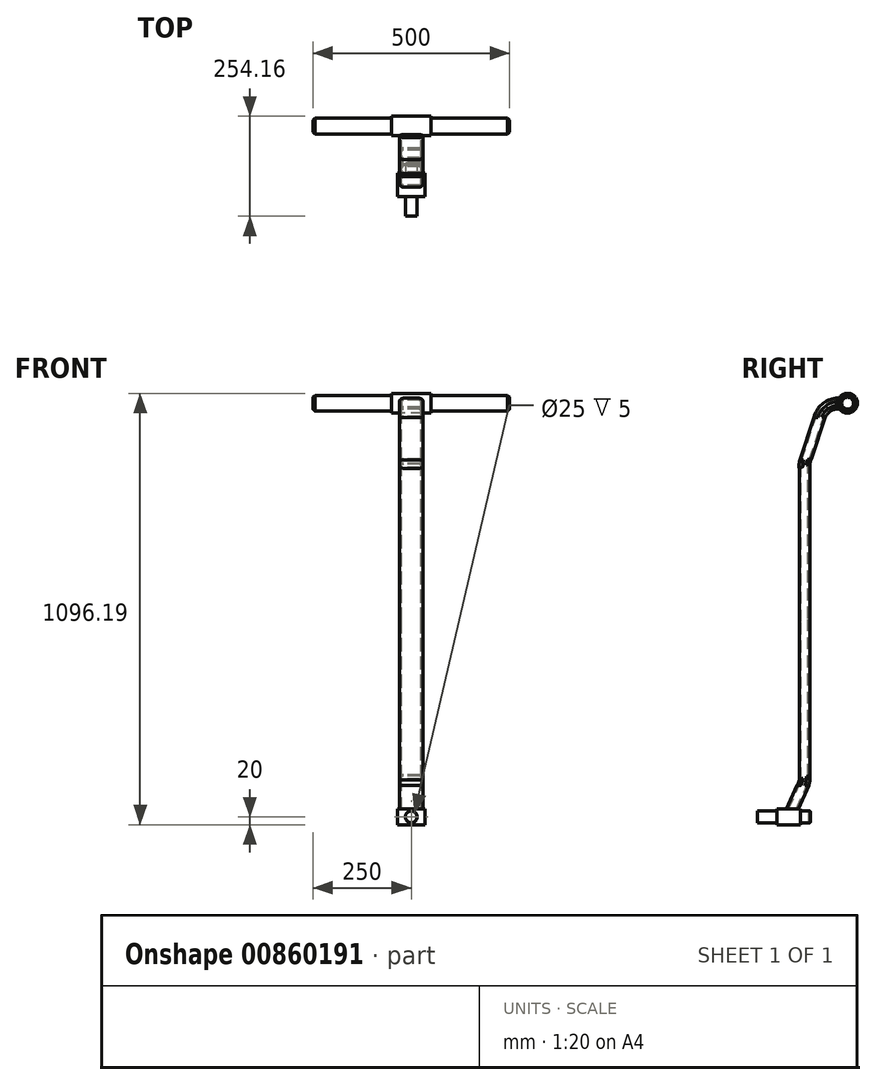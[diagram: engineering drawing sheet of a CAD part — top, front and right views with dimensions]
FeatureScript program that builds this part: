
annotation { "Feature Type Name" : "Feature", "Feature Type Description" : "" }
export const myFeature = defineFeature(function(context is Context, id is Id, definition is map)
    precondition{}
    {
        {
            var Q0;
            Q0=qCreatedBy(makeId("Top.planeOp"),FACE);
            var sketch = newSketch(context, id + "F0", { "sketchPlane" : qUnion([Q0])});
            skLineSegment(sketch, "E0.bottom", {"start": v(20, -15) * mm, "end": v(-20, -15) * mm});
            skLineSegment(sketch, "E0.top", {"start": v(20, 15) * mm, "end": v(-20, 15) * mm});
            skLineSegment(sketch, "E0.left", {"start": v(30, -5) * mm, "end": v(30, 5) * mm});
            skLineSegment(sketch, "E0.right", {"start": v(-30, -5) * mm, "end": v(-30, 5) * mm});
            skPoint(sketch, "E0.middle", {"position": v(0, 0) * mm});
            skPoint(sketch, "E1.visualSharp", {"position": v(-30, 15) * mm});
            skArc(sketch, "E1.filletArc", {"start": v(-20, 15) * mm, "mid": v(-27.07, 12.07) * mm, "end": v(-30, 5) * mm});
            skPoint(sketch, "E2.visualSharp", {"position": v(-30, -15) * mm});
            skArc(sketch, "E2.filletArc", {"start": v(-30, -5) * mm, "mid": v(-27.07, -12.07) * mm, "end": v(-20, -15) * mm});
            skPoint(sketch, "E3.visualSharp", {"position": v(30, -15) * mm});
            skArc(sketch, "E3.filletArc", {"start": v(20, -15) * mm, "mid": v(27.07, -12.07) * mm, "end": v(30, -5) * mm});
            skPoint(sketch, "E4.visualSharp", {"position": v(30, 15) * mm});
            skArc(sketch, "E4.filletArc", {"start": v(30, 5) * mm, "mid": v(27.07, 12.07) * mm, "end": v(20, 15) * mm});
            skLineSegment(sketch, "E5.bottom", {"start": v(20, 10) * mm, "end": v(-20, 10) * mm});
            skLineSegment(sketch, "E5.top", {"start": v(20, -10) * mm, "end": v(-20, -10) * mm});
            skLineSegment(sketch, "E5.left", {"start": v(25, 5) * mm, "end": v(25, -5) * mm});
            skLineSegment(sketch, "E5.right", {"start": v(-25, 5) * mm, "end": v(-25, -5) * mm});
            skPoint(sketch, "E6.visualSharp", {"position": v(-25, 10) * mm});
            skArc(sketch, "E6.filletArc", {"start": v(-20, 10) * mm, "mid": v(-23.54, 8.54) * mm, "end": v(-25, 5) * mm});
            skPoint(sketch, "E7.visualSharp", {"position": v(-25, -10) * mm});
            skArc(sketch, "E7.filletArc", {"start": v(-25, -5) * mm, "mid": v(-23.54, -8.54) * mm, "end": v(-20, -10) * mm});
            skPoint(sketch, "E8.visualSharp", {"position": v(25, -10) * mm});
            skArc(sketch, "E8.filletArc", {"start": v(20, -10) * mm, "mid": v(23.54, -8.54) * mm, "end": v(25, -5) * mm});
            skPoint(sketch, "E9.visualSharp", {"position": v(25, 10) * mm});
            skArc(sketch, "E9.filletArc", {"start": v(25, 5) * mm, "mid": v(23.54, 8.54) * mm, "end": v(20, 10) * mm});
            skSolve(sketch);
        }
        {
            var Q0;
            Q0=qCreatedBy(makeId("Right.planeOp"),FACE);
            var sketch = newSketch(context, id + "F1", { "sketchPlane" : qUnion([Q0])});
            skLineSegment(sketch, "E10", {"start": v(0, 0) * mm, "end": v(35.63, 79.56) * mm});
            skLineSegment(sketch, "E11", {"start": v(40, 100) * mm, "end": v(40, 500) * mm});
            skPoint(sketch, "E12.visualSharp", {"position": v(40, 89.31) * mm});
            skArc(sketch, "E12.filletArc", {"start": v(35.63, 79.56) * mm, "mid": v(38.9, 89.55) * mm, "end": v(40, 100) * mm});
            skLineSegment(sketch, "E13", {"start": v(40, 500) * mm, "end": v(40, 891.89) * mm});
            skLineSegment(sketch, "E14", {"start": v(42.57, 907.7) * mm, "end": v(78.6, 1015.81) * mm});
            skLineSegment(sketch, "E15", {"start": v(126.04, 1050) * mm, "end": v(150, 1050) * mm});
            skPoint(sketch, "E16.visualSharp", {"position": v(40, 900) * mm});
            skArc(sketch, "E16.filletArc", {"start": v(42.57, 907.7) * mm, "mid": v(40.65, 899.9) * mm, "end": v(40, 891.89) * mm});
            skPoint(sketch, "E17.visualSharp", {"position": v(90, 1050) * mm});
            skArc(sketch, "E17.filletArc", {"start": v(126.04, 1050) * mm, "mid": v(96.8, 1040.56) * mm, "end": v(78.6, 1015.81) * mm});
            skSolve(sketch);
        }
        {
            var Q0;
            Q0 = qSketchRegion(id + "F0", true);
            var Q1;
            Q1 = qConstructionFilter(qBodyType(qCreatedBy(id + "F1" ,EDGE), BodyType.WIRE), ConstructionObject.NO);
            sweep(context, id + "F2", {"profiles" : qUnion([Q0]), "path" : qUnion([Q1])});
        }
        {
            var Q0;
            Q0=qCreatedBy(makeId("Right.planeOp"),FACE);
            var sketch = newSketch(context, id + "F3", { "sketchPlane" : qUnion([Q0])});
            skCircle(sketch, "E18", {"center": v(149.16, 1051.19) * mm, "radius": 25 * mm});
            skSolve(sketch);
        }
        {
            var Q0;
            Q0 = qSketchRegion(id + "F3", true);
            extrude(context, id + "F4", {"entities" : qUnion([Q0]), "operationType" : NewBodyOperationType.ADD, "endBound" : BoundingType.SYMMETRIC, "depth" : 100 * mm, "offsetDistance" : 25 * mm});
        }
        {
            var Q0;
            Q0=qCreatedBy(makeId("Right.planeOp"),FACE);
            var sketch = newSketch(context, id + "F5", { "sketchPlane" : qUnion([Q0])});
            skCircle(sketch, "E19", {"center": v(149.16, 1051.19) * mm, "radius": 20 * mm});
            skSolve(sketch);
        }
        {
            var Q0;
            Q0 = qSketchRegion(id + "F5", true);
            extrude(context, id + "F6", {"entities" : qUnion([Q0]), "operationType" : NewBodyOperationType.ADD, "endBound" : BoundingType.SYMMETRIC, "depth" : 500 * mm, "offsetDistance" : 25 * mm});
        }
        {
            var Q0;
            Q0=makeQuery(id+"F6.opExtrude","CAP_EDGE",EDGE,{"disambiguationData":[OSD([sQuery(id+"F5.wireOp",EDGE,"E19")])],"isStart":true});
            var Q1;
            Q1=makeQuery(id+"F6.opExtrude","CAP_EDGE",EDGE,{"disambiguationData":[OSD([sQuery(id+"F5.wireOp",EDGE,"E19")])],"isStart":false});
            chamfer(context, id + "F7", {"entities" : qUnion([Q0, Q1]), "width" : 5 * mm, "tangentPropagation" : true});
        }
        {
            var Q0;
            Q0=qCreatedBy(makeId("Right.planeOp"),FACE);
            var sketch = newSketch(context, id + "F8", { "sketchPlane" : qUnion([Q0])});
            skLineSegment(sketch, "E20.bottom", {"start": v(30, -20) * mm, "end": v(-30, -20) * mm});
            skLineSegment(sketch, "E20.top", {"start": v(30, 20) * mm, "end": v(-30, 20) * mm});
            skLineSegment(sketch, "E20.left", {"start": v(30, -20) * mm, "end": v(30, 20) * mm});
            skLineSegment(sketch, "E20.right", {"start": v(-30, -20) * mm, "end": v(-30, 20) * mm});
            skPoint(sketch, "E20.middle", {"position": v(0, 0) * mm});
            skSolve(sketch);
        }
        {
            var Q0;
            Q0 = qSketchRegion(id + "F8", true);
            extrude(context, id + "F9", {"entities" : qUnion([Q0]), "operationType" : NewBodyOperationType.ADD, "endBound" : BoundingType.SYMMETRIC, "depth" : 70 * mm, "offsetDistance" : 25 * mm});
        }
        {
            var Q0;
            Q0=makeQuery(id+"F9.opExtrude","SWEPT_FACE",FACE,{"disambiguationData":[OSD([sQuery(id+"F8.wireOp",EDGE,"E20.left")])]});
            var sketch = newSketch(context, id + "F10", { "sketchPlane" : qUnion([Q0])});
            skCircle(sketch, "E21", {"center": v(0, 0) * mm, "radius": 15 * mm});
            skSolve(sketch);
        }
        {
            var Q0;
            Q0 = qSketchRegion(id + "F10", true);
            extrude(context, id + "F11", {"entities" : qUnion([Q0]), "operationType" : NewBodyOperationType.ADD, "depth" : 25 * mm, "offsetDistance" : 25 * mm});
        }
        {
            var Q0;
            Q0=makeQuery(id+"F9.opExtrude","SWEPT_FACE",FACE,{"disambiguationData":[OSD([sQuery(id+"F8.wireOp",EDGE,"E20.right")])]});
            var sketch = newSketch(context, id + "F12", { "sketchPlane" : qUnion([Q0])});
            skCircle(sketch, "E22", {"center": v(0, 0) * mm, "radius": 15 * mm});
            skSolve(sketch);
        }
        {
            var Q0;
            Q0 = qSketchRegion(id + "F12", true);
            extrude(context, id + "F13", {"entities" : qUnion([Q0]), "operationType" : NewBodyOperationType.ADD, "depth" : 50 * mm, "offsetDistance" : 25 * mm});
        }
        {
            var Q0;
            Q0=makeQuery(id+"F11.opExtrude","CAP_FACE",FACE,{"disambiguationData":[OSD([sQuery(id+"F10.wireOp",EDGE,"E21")])],"isStart":false});
            var sketch = newSketch(context, id + "F14", { "sketchPlane" : qUnion([Q0])});
            skCircle(sketch, "E23", {"center": v(0, 0) * mm, "radius": 12.5 * mm});
            skSolve(sketch);
        }
        {
            var Q0;
            Q0 = qSketchRegion(id + "F14", true);
            extrude(context, id + "F15", {"entities" : qUnion([Q0]), "operationType" : NewBodyOperationType.REMOVE, "oppositeDirection" : true, "depth" : 5 * mm, "offsetDistance" : 25 * mm});
        }
        {
            var Q0;
            Q0=makeQuery(id+"F11.opExtrude","CAP_EDGE",EDGE,{"disambiguationData":[OSD([sQuery(id+"F10.wireOp",EDGE,"E21")])],"isStart":false});
            fillet(context, id + "F16", {"entities" : qUnion([Q0]), "radius" : 2 * mm, "tangentPropagation" : true, "allowEdgeOverflow" : false});
        }
    });
